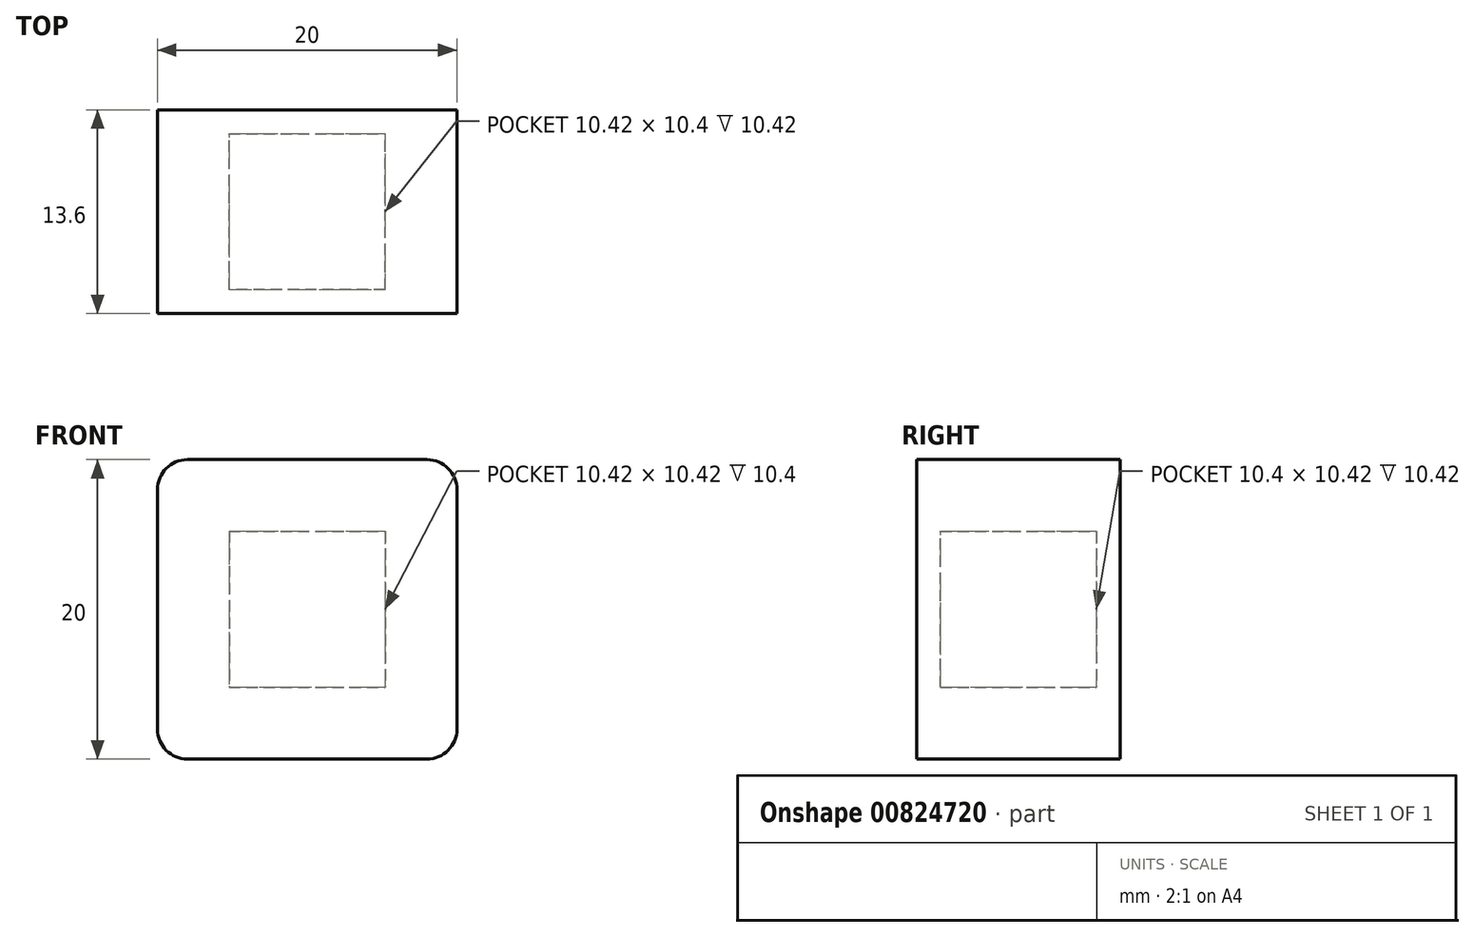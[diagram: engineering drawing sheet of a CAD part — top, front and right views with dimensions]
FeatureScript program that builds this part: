
annotation { "Feature Type Name" : "Feature", "Feature Type Description" : "" }
export const myFeature = defineFeature(function(context is Context, id is Id, definition is map)
    precondition{}
    {
        {
            var Q0;
            Q0=qCreatedBy(makeId("Front.planeOp"),FACE);
            var sketch = newSketch(context, id + "F0", { "sketchPlane" : qUnion([Q0])});
            skLineSegment(sketch, "E0.bottom", {"start": v(10, -10) * mm, "end": v(-10, -10) * mm});
            skLineSegment(sketch, "E0.top", {"start": v(10, 10) * mm, "end": v(-10, 10) * mm});
            skLineSegment(sketch, "E0.left", {"start": v(10, -10) * mm, "end": v(10, 10) * mm});
            skLineSegment(sketch, "E0.right", {"start": v(-10, -10) * mm, "end": v(-10, 10) * mm});
            skPoint(sketch, "E0.middle", {"position": v(0, 0) * mm});
            skLineSegment(sketch, "E1.bottom", {"start": v(5.2, -5.2) * mm, "end": v(-5.21, -5.21) * mm});
            skLineSegment(sketch, "E1.top", {"start": v(5.2, 5.21) * mm, "end": v(-5.2, 5.2) * mm});
            skLineSegment(sketch, "E1.left", {"start": v(5.2, -5.2) * mm, "end": v(5.2, 5.21) * mm});
            skLineSegment(sketch, "E1.right", {"start": v(-5.2, -5.21) * mm, "end": v(-5.2, 5.2) * mm});
            skSolve(sketch);
        }
        {
            var Q0;
            Q0=makeQuery(id+"F0.imprint","IMPRINT",FACE,{"disambiguationData":[TD([[makeQuery(id+"F0.imprint","IMPRINT",EDGE,{"derivedFrom":sQuery(id+"F0.wireOp",EDGE,"E0.bottom")}),-1.0]])]});
            var Q1;
            Q1=makeQuery(id+"F0.imprint","IMPRINT",FACE,{"disambiguationData":[TD([[makeQuery(id+"F0.imprint","IMPRINT",EDGE,{"derivedFrom":sQuery(id+"F0.wireOp",EDGE,"E1.bottom")}),-1.0]])]});
            extrude(context, id + "F1", {"entities" : qUnion([Q0, Q1]), "depth" : 1.6 * mm, "offsetDistance" : 25 * mm});
        }
        {
            var Q0;
            Q0=makeQuery(id+"F0.imprint","IMPRINT",FACE,{"disambiguationData":[TD([[makeQuery(id+"F0.imprint","IMPRINT",EDGE,{"derivedFrom":sQuery(id+"F0.wireOp",EDGE,"E0.bottom")}),-1.0]])]});
            extrude(context, id + "F2", {"entities" : qUnion([Q0]), "operationType" : NewBodyOperationType.ADD, "depth" : 12 * mm, "offsetDistance" : 25 * mm});
        }
        {
            var Q0;
            Q0=makeQuery(id+"F2.opExtrude","CAP_FACE",FACE,{"disambiguationData":[OSD([sQuery(id+"F0.wireOp",EDGE,"E0.bottom"),sQuery(id+"F0.wireOp",EDGE,"E0.top"),sQuery(id+"F0.wireOp",EDGE,"E0.left"),sQuery(id+"F0.wireOp",EDGE,"E0.right"),sQuery(id+"F0.wireOp",EDGE,"E1.bottom"),sQuery(id+"F0.wireOp",EDGE,"E1.top"),sQuery(id+"F0.wireOp",EDGE,"E1.left"),sQuery(id+"F0.wireOp",EDGE,"E1.right")])],"isStart":false});
            var sketch = newSketch(context, id + "F3", { "sketchPlane" : qUnion([Q0])});
            skLineSegment(sketch, "E2.0", {"start": v(10, 10) * mm, "end": v(-10, 10) * mm});
            skLineSegment(sketch, "E3.0", {"start": v(-10, -10) * mm, "end": v(-10, 10) * mm});
            skLineSegment(sketch, "E4.0", {"start": v(10, -10) * mm, "end": v(10, 10) * mm});
            skLineSegment(sketch, "E5.0", {"start": v(10, -10) * mm, "end": v(-10, -10) * mm});
            skSolve(sketch);
        }
        {
            var Q0;
            Q0=makeQuery(id+"F3.imprint","IMPRINT",FACE,{"disambiguationData":[TD([[makeQuery(id+"F3.imprint","IMPRINT",EDGE,{"derivedFrom":sQuery(id+"F3.wireOp",EDGE,"E2.0")}),1.0]])]});
            var Q1;
            Q1=makeQuery(id+"F3.imprint","IMPRINT",FACE,{"disambiguationData":[TD([[makeQuery(id+"F3.imprint","IMPRINT",EDGE,{"derivedFrom":makeQuery(id+"F2.opExtrude","CAP_EDGE",EDGE,{"disambiguationData":[OSD([sQuery(id+"F0.wireOp",EDGE,"E1.bottom")])],"isStart":false})}),-1.0]])]});
            extrude(context, id + "F4", {"entities" : qUnion([Q0, Q1]), "operationType" : NewBodyOperationType.ADD, "depth" : 1.6 * mm, "offsetDistance" : 25 * mm});
        }
        {
            var Q0;
            {var subQ0=sQuery(id+"F0.wireOp",EDGE,"E0.right");var subQ1=sQuery(id+"F0.wireOp",EDGE,"E0.bottom");Q0=makeQuery(id+"F4.boolean.opBoolean","MERGE",EDGE,{"derivedFrom":[makeQuery(id+"F2.boolean.opBoolean","MERGE",EDGE,{"derivedFrom":[makeQuery(id+"F1.opExtrude","SWEPT_EDGE",EDGE,{"disambiguationData":[OSD([subQ1,subQ0])]}),makeQuery(id+"F2.opExtrude","SWEPT_EDGE",EDGE,{"disambiguationData":[OSD([subQ1,subQ0])]})]}),makeQuery(id+"F4.opExtrude","SWEPT_EDGE",EDGE,{"disambiguationData":[OSD([sQuery(id+"F3.wireOp",EDGE,"E3.0"),sQuery(id+"F3.wireOp",EDGE,"E5.0")])]})]});}
            var Q1;
            {var subQ0=sQuery(id+"F0.wireOp",EDGE,"E0.left");var subQ1=sQuery(id+"F0.wireOp",EDGE,"E0.bottom");Q1=makeQuery(id+"F4.boolean.opBoolean","MERGE",EDGE,{"derivedFrom":[makeQuery(id+"F2.boolean.opBoolean","MERGE",EDGE,{"derivedFrom":[makeQuery(id+"F1.opExtrude","SWEPT_EDGE",EDGE,{"disambiguationData":[OSD([subQ1,subQ0])]}),makeQuery(id+"F2.opExtrude","SWEPT_EDGE",EDGE,{"disambiguationData":[OSD([subQ1,subQ0])]})]}),makeQuery(id+"F4.opExtrude","SWEPT_EDGE",EDGE,{"disambiguationData":[OSD([sQuery(id+"F3.wireOp",EDGE,"E4.0"),sQuery(id+"F3.wireOp",EDGE,"E5.0")])]})]});}
            var Q2;
            {var subQ0=sQuery(id+"F0.wireOp",EDGE,"E0.left");var subQ1=sQuery(id+"F0.wireOp",EDGE,"E0.top");Q2=makeQuery(id+"F4.boolean.opBoolean","MERGE",EDGE,{"derivedFrom":[makeQuery(id+"F2.boolean.opBoolean","MERGE",EDGE,{"derivedFrom":[makeQuery(id+"F1.opExtrude","SWEPT_EDGE",EDGE,{"disambiguationData":[OSD([subQ1,subQ0])]}),makeQuery(id+"F2.opExtrude","SWEPT_EDGE",EDGE,{"disambiguationData":[OSD([subQ1,subQ0])]})]}),makeQuery(id+"F4.opExtrude","SWEPT_EDGE",EDGE,{"disambiguationData":[OSD([sQuery(id+"F3.wireOp",EDGE,"E2.0"),sQuery(id+"F3.wireOp",EDGE,"E4.0")])]})]});}
            var Q3;
            {var subQ0=sQuery(id+"F0.wireOp",EDGE,"E0.right");var subQ1=sQuery(id+"F0.wireOp",EDGE,"E0.top");Q3=makeQuery(id+"F4.boolean.opBoolean","MERGE",EDGE,{"derivedFrom":[makeQuery(id+"F2.boolean.opBoolean","MERGE",EDGE,{"derivedFrom":[makeQuery(id+"F1.opExtrude","SWEPT_EDGE",EDGE,{"disambiguationData":[OSD([subQ1,subQ0])]}),makeQuery(id+"F2.opExtrude","SWEPT_EDGE",EDGE,{"disambiguationData":[OSD([subQ1,subQ0])]})]}),makeQuery(id+"F4.opExtrude","SWEPT_EDGE",EDGE,{"disambiguationData":[OSD([sQuery(id+"F3.wireOp",EDGE,"E2.0"),sQuery(id+"F3.wireOp",EDGE,"E3.0")])]})]});}
            fillet(context, id + "F5", {"entities" : qUnion([Q0, Q1, Q2, Q3]), "radius" : 2 * mm, "tangentPropagation" : true, "allowEdgeOverflow" : false});
        }
    });
